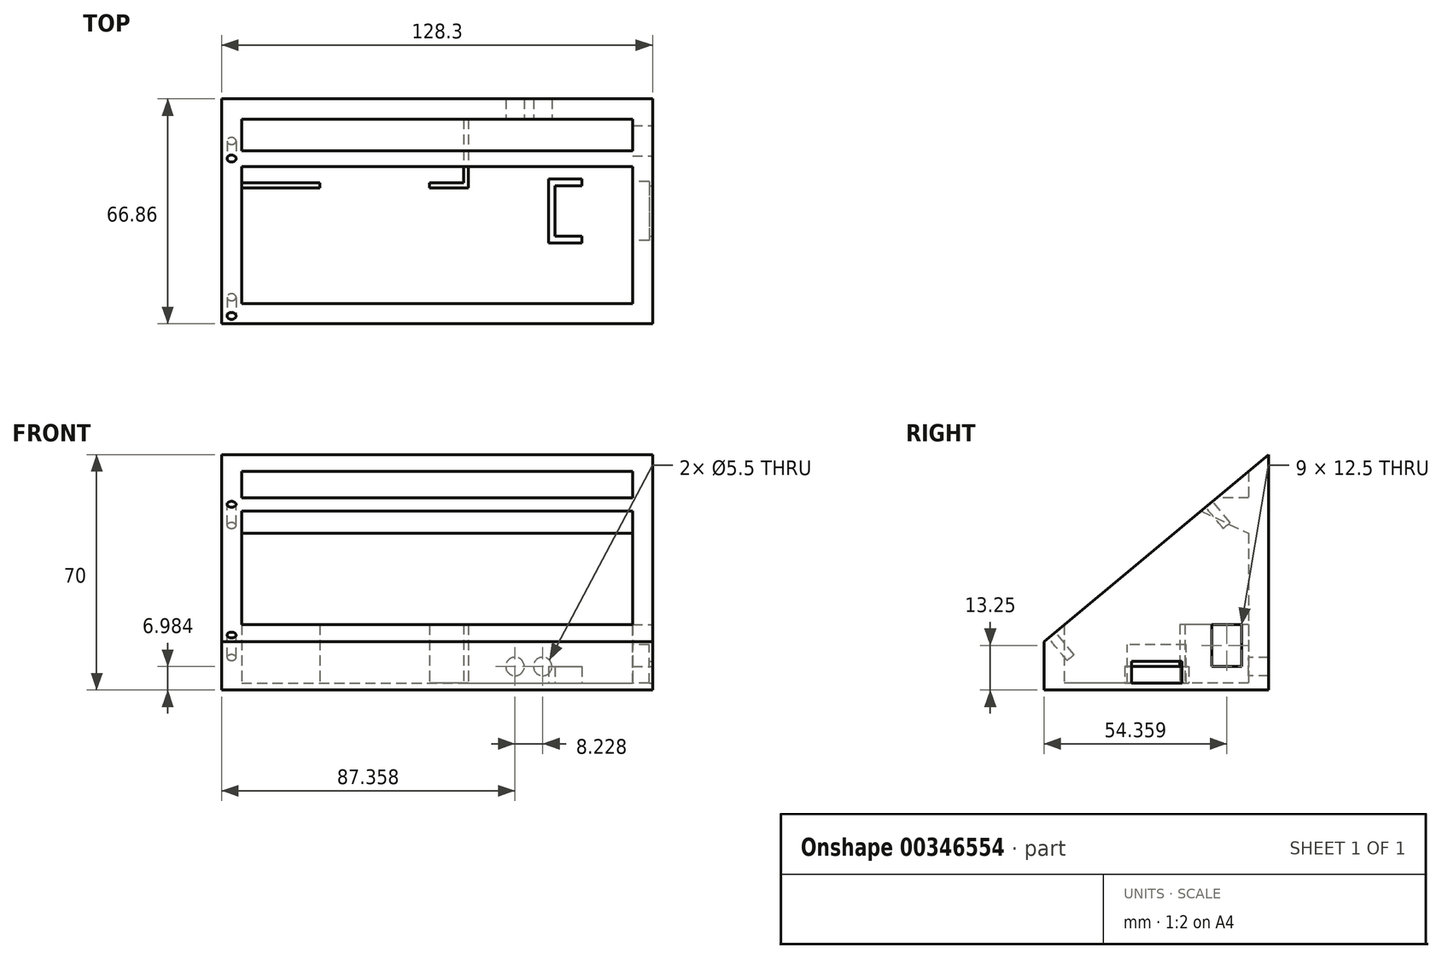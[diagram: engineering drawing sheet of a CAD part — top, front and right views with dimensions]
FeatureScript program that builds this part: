
annotation { "Feature Type Name" : "Feature", "Feature Type Description" : "" }
export const myFeature = defineFeature(function(context is Context, id is Id, definition is map)
    precondition{}
    {
        {
            var Q0;
            Q0=qCreatedBy(makeId("Top.planeOp"),FACE);
            var sketch = newSketch(context, id + "F0", { "sketchPlane" : qUnion([Q0])});
            skLineSegment(sketch, "E0.bottom", {"start": v(-64.15, -33.43) * mm, "end": v(64.15, -33.43) * mm});
            skLineSegment(sketch, "E0.top", {"start": v(-64.15, 33.43) * mm, "end": v(64.15, 33.43) * mm});
            skLineSegment(sketch, "E0.left", {"start": v(-64.15, -33.43) * mm, "end": v(-64.15, 33.43) * mm});
            skLineSegment(sketch, "E0.right", {"start": v(64.15, -33.43) * mm, "end": v(64.15, 33.43) * mm});
            skPoint(sketch, "E0.middle", {"position": v(0, 0) * mm});
            skLineSegment(sketch, "E1.bottom", {"start": v(-58.15, 27.43) * mm, "end": v(58.15, 27.43) * mm});
            skLineSegment(sketch, "E1.top", {"start": v(-58.15, -27.43) * mm, "end": v(58.15, -27.43) * mm});
            skLineSegment(sketch, "E1.left", {"start": v(-58.15, 27.43) * mm, "end": v(-58.15, -27.43) * mm});
            skLineSegment(sketch, "E1.right", {"start": v(58.15, 27.43) * mm, "end": v(58.15, -27.43) * mm});
            skSolve(sketch);
        }
        {
            var Q0;
            Q0=makeQuery(id+"F0.imprint","IMPRINT",FACE,{"disambiguationData":[TD([[makeQuery(id+"F0.imprint","IMPRINT",EDGE,{"derivedFrom":sQuery(id+"F0.wireOp",EDGE,"E0.bottom")}),1.0]])]});
            extrude(context, id + "F1", {"entities" : qUnion([Q0]), "depth" : 70 * mm});
        }
        {
            var Q0;
            Q0=makeQuery(id+"F0.imprint","IMPRINT",FACE,{"disambiguationData":[TD([[makeQuery(id+"F0.imprint","IMPRINT",EDGE,{"derivedFrom":sQuery(id+"F0.wireOp",EDGE,"E1.bottom")}),-1.0]])]});
            extrude(context, id + "F2", {"entities" : qUnion([Q0]), "operationType" : NewBodyOperationType.ADD, "depth" : 2 * mm});
        }
        {
            var Q0;
            Q0=makeQuery(id+"F1.opExtrude","SWEPT_FACE",FACE,{"disambiguationData":[OSD([sQuery(id+"F0.wireOp",EDGE,"E0.right")])]});
            var sketch = newSketch(context, id + "F3", { "sketchPlane" : qUnion([Q0])});
            skLineSegment(sketch, "E2", {"start": v(33.43, 70) * mm, "end": v(-33.43, 14.43) * mm});
            skLineSegment(sketch, "E3", {"start": v(-33.43, 14.43) * mm, "end": v(-33.43, 70) * mm});
            skLineSegment(sketch, "E4", {"start": v(-33.43, 70) * mm, "end": v(33.43, 70) * mm});
            skSolve(sketch);
        }
        {
            var Q0;
            Q0=makeQuery(id+"F3.imprint","IMPRINT",FACE,{"disambiguationData":[TD([[makeQuery(id+"F3.imprint","IMPRINT",EDGE,{"derivedFrom":sQuery(id+"F3.wireOp",EDGE,"E2")}),-1.0]])]});
            extrude(context, id + "F4", {"entities" : qUnion([Q0]), "operationType" : NewBodyOperationType.REMOVE, "oppositeDirection" : true, "depth" : 130 * mm});
        }
        {
            var Q0;
            Q0=makeQuery(id+"F1.opExtrude","SWEPT_FACE",FACE,{"disambiguationData":[OSD([sQuery(id+"F0.wireOp",EDGE,"E0.right")])]});
            var sketch = newSketch(context, id + "F5", { "sketchPlane" : qUnion([Q0])});
            skLineSegment(sketch, "E5.bottom", {"start": v(25.43, 7) * mm, "end": v(16.43, 7) * mm});
            skLineSegment(sketch, "E5.top", {"start": v(25.43, 19.5) * mm, "end": v(16.43, 19.5) * mm});
            skLineSegment(sketch, "E5.left", {"start": v(25.43, 7) * mm, "end": v(25.43, 19.5) * mm});
            skLineSegment(sketch, "E5.right", {"start": v(16.43, 7) * mm, "end": v(16.43, 19.5) * mm});
            skPoint(sketch, "E5.middle", {"position": v(20.93, 13.25) * mm});
            skLineSegment(sketch, "E6.bottom", {"start": v(7.6, 2) * mm, "end": v(-7.4, 2) * mm});
            skLineSegment(sketch, "E6.top", {"start": v(7.6, 8.5) * mm, "end": v(-7.4, 8.5) * mm});
            skLineSegment(sketch, "E6.left", {"start": v(7.6, 2) * mm, "end": v(7.6, 8.5) * mm});
            skLineSegment(sketch, "E6.right", {"start": v(-7.4, 2) * mm, "end": v(-7.4, 8.5) * mm});
            skPoint(sketch, "E6.middle", {"position": v(0.1, 5.25) * mm});
            skSolve(sketch);
        }
        {
            var Q0;
            Q0=makeQuery(id+"F5.imprint","IMPRINT",FACE,{"disambiguationData":[TD([[makeQuery(id+"F5.imprint","IMPRINT",EDGE,{"derivedFrom":sQuery(id+"F5.wireOp",EDGE,"E5.bottom")}),-1.0]])]});
            extrude(context, id + "F6", {"entities" : qUnion([Q0]), "operationType" : NewBodyOperationType.REMOVE, "oppositeDirection" : true, "depth" : 7 * mm});
        }
        {
            var Q0;
            Q0=makeQuery(id+"F5.imprint","IMPRINT",FACE,{"disambiguationData":[TD([[makeQuery(id+"F5.imprint","IMPRINT",EDGE,{"derivedFrom":sQuery(id+"F5.wireOp",EDGE,"E6.bottom")}),-1.0]])]});
            extrude(context, id + "F7", {"entities" : qUnion([Q0]), "operationType" : NewBodyOperationType.REMOVE, "oppositeDirection" : true, "depth" : 7 * mm});
        }
        {
            var Q0;
            Q0=makeQuery(id+"F1.opExtrude","SWEPT_FACE",FACE,{"disambiguationData":[OSD([sQuery(id+"F0.wireOp",EDGE,"E1.right")])]});
            var sketch = newSketch(context, id + "F8", { "sketchPlane" : qUnion([Q0])});
            skLineSegment(sketch, "E7.bottom", {"start": v(-8.84, 2) * mm, "end": v(8.66, 2) * mm});
            skLineSegment(sketch, "E7.top", {"start": v(-8.84, 13.5) * mm, "end": v(8.66, 13.5) * mm});
            skLineSegment(sketch, "E7.left", {"start": v(-8.84, 2) * mm, "end": v(-8.84, 13.5) * mm});
            skLineSegment(sketch, "E7.right", {"start": v(8.66, 2) * mm, "end": v(8.66, 13.5) * mm});
            skSolve(sketch);
        }
        {
            var Q0;
            Q0=makeQuery(id+"F8.imprint","IMPRINT",FACE,{"disambiguationData":[TD([[makeQuery(id+"F8.imprint","IMPRINT",EDGE,{"derivedFrom":sQuery(id+"F8.wireOp",EDGE,"E7.top")}),-1.0]])]});
            extrude(context, id + "F9", {"entities" : qUnion([Q0]), "operationType" : NewBodyOperationType.REMOVE, "oppositeDirection" : true, "depth" : 5 * mm});
        }
        {
            var Q0;
            {var subQ0=sQuery(id+"F8.wireOp",EDGE,"E7.bottom");var subQ1=makeQuery(id+"F7.opExtrude","SWEPT_FACE",FACE,{"disambiguationData":[OSD([sQuery(id+"F5.wireOp",EDGE,"E6.right")])]});var subQ2=sQuery(id+"F0.wireOp",EDGE,"E1.right");var subQ3=makeQuery(id+"F1.opExtrude","SWEPT_FACE",FACE,{"disambiguationData":[OSD([subQ2])]});var subQ4=subQ3;var subQ5=makeQuery(id+"F7.opExtrude","SWEPT_FACE",FACE,{"disambiguationData":[OSD([sQuery(id+"F5.wireOp",EDGE,"E6.bottom")])]});var subQ6=sQuery(id+"F0.wireOp",EDGE,"E1.top");var subQ7=sQuery(id+"F0.wireOp",EDGE,"E1.bottom");var subQ8=makeQuery(id+"F2.opExtrude","CAP_FACE",FACE,{"disambiguationData":[OSD([subQ7,subQ6,sQuery(id+"F0.wireOp",EDGE,"E1.left"),subQ2])],"isStart":false});var subQ10=makeQuery(id+"F7.opExtrude","SWEPT_FACE",FACE,{"disambiguationData":[OSD([sQuery(id+"F5.wireOp",EDGE,"E6.left")])]});Q0=makeQuery(id+"F9.boolean.opBoolean","MERGE",FACE,{"derivedFrom":[makeQuery(id+"F7.boolean.opBoolean","MERGE",FACE,{"derivedFrom":[subQ8,subQ5]}),makeQuery(id+"F9.opExtrude","SWEPT_FACE",FACE,{"disambiguationData":[OSD([subQ0]),TDD([makeQuery(id+"F8.imprint","IMPRINT",EDGE,{"disambiguationData":[TD([[makeQuery(id+"F8.imprint","INTERSECT",VERTEX,{"derivedFrom":[makeQuery(id+"F7.boolean.opBoolean","INTERSECT",EDGE,{"derivedFrom":[subQ4,subQ10]}),subQ0]}),1.0]])],"derivedFrom":subQ0})])]}),makeQuery(id+"F9.opExtrude","SWEPT_FACE",FACE,{"disambiguationData":[OSD([subQ0]),TDD([makeQuery(id+"F8.imprint","IMPRINT",EDGE,{"disambiguationData":[TD([[makeQuery(id+"F8.imprint","INTERSECT",VERTEX,{"derivedFrom":[makeQuery(id+"F7.boolean.opBoolean","INTERSECT",EDGE,{"derivedFrom":[subQ4,subQ1]}),subQ0]}),-1.0]])],"derivedFrom":subQ0})])]})]});}
            var sketch = newSketch(context, id + "F10", { "sketchPlane" : qUnion([Q0])});
            skLineSegment(sketch, "E8.left", {"start": v(33.15, 7.6) * mm, "end": v(33.15, -7.4) * mm});
            skLineSegment(sketch, "E8.right", {"start": v(35.15, 7.6) * mm, "end": v(35.15, -7.4) * mm});
            skLineSegment(sketch, "E9.bottom", {"start": v(35.15, 7.6) * mm, "end": v(43.15, 7.6) * mm});
            skLineSegment(sketch, "E9.top", {"start": v(33.15, 9.6) * mm, "end": v(43.15, 9.6) * mm});
            skLineSegment(sketch, "E9.left", {"start": v(33.15, 7.6) * mm, "end": v(33.15, 9.6) * mm});
            skLineSegment(sketch, "E9.right", {"start": v(43.15, 7.6) * mm, "end": v(43.15, 9.6) * mm});
            skLineSegment(sketch, "E10.bottom", {"start": v(35.15, -7.4) * mm, "end": v(43.15, -7.4) * mm});
            skLineSegment(sketch, "E10.top", {"start": v(33.15, -9.4) * mm, "end": v(43.15, -9.4) * mm});
            skLineSegment(sketch, "E10.left", {"start": v(33.15, -7.4) * mm, "end": v(33.15, -9.4) * mm});
            skLineSegment(sketch, "E10.right", {"start": v(43.15, -7.4) * mm, "end": v(43.15, -9.4) * mm});
            skLineSegment(sketch, "E11", {"start": v(64.15, 7.6) * mm, "end": v(5.36, 7.6) * mm, "construction": true});
            skLineSegment(sketch, "E12", {"start": v(64.15, -7.4) * mm, "end": v(18.59, -7.4) * mm, "construction": true});
            skSolve(sketch);
        }
        {
            var Q0;
            Q0=makeQuery(id+"F10.imprint","IMPRINT",FACE,{"disambiguationData":[TD([[makeQuery(id+"F10.imprint","IMPRINT",EDGE,{"derivedFrom":sQuery(id+"F10.wireOp",EDGE,"E8.left")}),1.0]])]});
            extrude(context, id + "F11", {"entities" : qUnion([Q0]), "operationType" : NewBodyOperationType.ADD, "depth" : 5 * mm});
        }
        {
            var Q0;
            {var subQ0=sQuery(id+"F8.wireOp",EDGE,"E7.bottom");var subQ1=makeQuery(id+"F7.opExtrude","SWEPT_FACE",FACE,{"disambiguationData":[OSD([sQuery(id+"F5.wireOp",EDGE,"E6.right")])]});var subQ2=sQuery(id+"F0.wireOp",EDGE,"E1.right");var subQ3=makeQuery(id+"F1.opExtrude","SWEPT_FACE",FACE,{"disambiguationData":[OSD([subQ2])]});var subQ4=subQ3;var subQ5=makeQuery(id+"F7.opExtrude","SWEPT_FACE",FACE,{"disambiguationData":[OSD([sQuery(id+"F5.wireOp",EDGE,"E6.bottom")])]});var subQ6=sQuery(id+"F0.wireOp",EDGE,"E1.top");var subQ7=sQuery(id+"F0.wireOp",EDGE,"E1.bottom");var subQ8=makeQuery(id+"F2.opExtrude","CAP_FACE",FACE,{"disambiguationData":[OSD([subQ7,subQ6,sQuery(id+"F0.wireOp",EDGE,"E1.left"),subQ2])],"isStart":false});var subQ10=makeQuery(id+"F7.opExtrude","SWEPT_FACE",FACE,{"disambiguationData":[OSD([sQuery(id+"F5.wireOp",EDGE,"E6.left")])]});Q0=makeQuery(id+"F9.boolean.opBoolean","MERGE",FACE,{"derivedFrom":[makeQuery(id+"F7.boolean.opBoolean","MERGE",FACE,{"derivedFrom":[subQ8,subQ5]}),makeQuery(id+"F9.opExtrude","SWEPT_FACE",FACE,{"disambiguationData":[OSD([subQ0]),TDD([makeQuery(id+"F8.imprint","IMPRINT",EDGE,{"disambiguationData":[TD([[makeQuery(id+"F8.imprint","INTERSECT",VERTEX,{"derivedFrom":[makeQuery(id+"F7.boolean.opBoolean","INTERSECT",EDGE,{"derivedFrom":[subQ4,subQ10]}),subQ0]}),1.0]])],"derivedFrom":subQ0})])]}),makeQuery(id+"F9.opExtrude","SWEPT_FACE",FACE,{"disambiguationData":[OSD([subQ0]),TDD([makeQuery(id+"F8.imprint","IMPRINT",EDGE,{"disambiguationData":[TD([[makeQuery(id+"F8.imprint","INTERSECT",VERTEX,{"derivedFrom":[makeQuery(id+"F7.boolean.opBoolean","INTERSECT",EDGE,{"derivedFrom":[subQ4,subQ1]}),subQ0]}),-1.0]])],"derivedFrom":subQ0})])]})]});}
            var sketch = newSketch(context, id + "F12", { "sketchPlane" : qUnion([Q0])});
            skLineSegment(sketch, "E13.bottom", {"start": v(-58.15, 6.93) * mm, "end": v(-34.93, 6.93) * mm});
            skLineSegment(sketch, "E13.top", {"start": v(-58.15, 8.43) * mm, "end": v(-34.93, 8.43) * mm});
            skLineSegment(sketch, "E13.left", {"start": v(-58.15, 8.43) * mm, "end": v(-58.15, 6.93) * mm});
            skLineSegment(sketch, "E13.right", {"start": v(-34.93, 8.43) * mm, "end": v(-34.93, 6.93) * mm});
            skLineSegment(sketch, "E14.bottom", {"start": v(7.85, 27.43) * mm, "end": v(9.35, 27.43) * mm});
            skLineSegment(sketch, "E14.left", {"start": v(7.85, 27.43) * mm, "end": v(7.85, 8.43) * mm});
            skLineSegment(sketch, "E14.right", {"start": v(9.35, 27.43) * mm, "end": v(9.35, 8.43) * mm});
            skLineSegment(sketch, "E15.bottom", {"start": v(7.85, 8.43) * mm, "end": v(-2.25, 8.43) * mm});
            skLineSegment(sketch, "E15.top", {"start": v(9.35, 6.93) * mm, "end": v(-2.25, 6.93) * mm});
            skLineSegment(sketch, "E15.left", {"start": v(9.35, 8.43) * mm, "end": v(9.35, 6.93) * mm});
            skLineSegment(sketch, "E15.right", {"start": v(-2.25, 8.43) * mm, "end": v(-2.25, 6.93) * mm});
            skSolve(sketch);
        }
        {
            var Q0;
            Q0=makeQuery(id+"F12.imprint","IMPRINT",FACE,{"disambiguationData":[TD([[makeQuery(id+"F12.imprint","IMPRINT",EDGE,{"derivedFrom":sQuery(id+"F12.wireOp",EDGE,"E13.bottom")}),1.0]])]});
            var Q1;
            Q1=makeQuery(id+"F12.imprint","IMPRINT",FACE,{"disambiguationData":[TD([[makeQuery(id+"F12.imprint","IMPRINT",EDGE,{"derivedFrom":sQuery(id+"F12.wireOp",EDGE,"E14.bottom")}),-1.0]])]});
            extrude(context, id + "F13", {"entities" : qUnion([Q0, Q1]), "operationType" : NewBodyOperationType.ADD, "depth" : 17.5 * mm});
        }
        {
            var Q0;
            Q0=makeQuery(id+"F4.boolean.opBoolean","COPY",FACE,{"derivedFrom":makeQuery(id+"F4.opExtrude","SWEPT_FACE",FACE,{"disambiguationData":[OSD([sQuery(id+"F3.wireOp",EDGE,"E2")])]})});
            cPlane(context, id + "F14", {"entities" : qUnion([Q0]), "cplaneType" : CPlaneType.OFFSET, "offset" : 0.8 * mm, "width" : 150 * mm, "height" : 150 * mm});
        }
        {
            var Q0;
            Q0=qCreatedBy(id+"F14.planeOp",FACE);
            var sketch = newSketch(context, id + "F15", { "sketchPlane" : qUnion([Q0])});
            skCircle(sketch, "E16", {"center": v(-61.15, 47.37) * mm, "radius": 1.35 * mm});
            skCircle(sketch, "E17", {"center": v(-61.15, -13.48) * mm, "radius": 1.35 * mm});
            skCircle(sketch, "E18.MirrorC", {"center": v(61.15, -13.48) * mm, "radius": 1.35 * mm});
            skCircle(sketch, "E19.MirrorC", {"center": v(61.15, 47.37) * mm, "radius": 1.35 * mm});
            skSolve(sketch);
        }
        {
            var Q0;
            Q0=makeQuery(id+"F15.imprint","IMPRINT",FACE,{"disambiguationData":[TD([[makeQuery(id+"F15.imprint","IMPRINT",EDGE,{"derivedFrom":sQuery(id+"F15.wireOp",EDGE,"E17")}),1.0]])]});
            var Q1;
            Q1=makeQuery(id+"F15.imprint","IMPRINT",FACE,{"disambiguationData":[TD([[makeQuery(id+"F15.imprint","IMPRINT",EDGE,{"derivedFrom":sQuery(id+"F15.wireOp",EDGE,"E18.MirrorC")}),-1.0]])]});
            extrude(context, id + "F16", {"entities" : qUnion([Q0, Q1]), "operationType" : NewBodyOperationType.REMOVE, "oppositeDirection" : true, "depth" : 9.5 * mm});
        }
        {
            var Q0;
            Q0=makeQuery(id+"F1.opExtrude","SWEPT_FACE",FACE,{"disambiguationData":[OSD([sQuery(id+"F0.wireOp",EDGE,"E0.right")])]});
            var sketch = newSketch(context, id + "F17", { "sketchPlane" : qUnion([Q0])});
            skLineSegment(sketch, "E20.bottom", {"start": v(92.05, 115.27) * mm, "end": v(-2.96, 115.27) * mm});
            skLineSegment(sketch, "E20.top", {"start": v(92.05, 57.17) * mm, "end": v(-2.96, 57.17) * mm});
            skLineSegment(sketch, "E20.left", {"start": v(92.05, 115.27) * mm, "end": v(92.05, 57.17) * mm});
            skLineSegment(sketch, "E20.right", {"start": v(-2.96, 115.27) * mm, "end": v(-2.96, 57.17) * mm});
            skPoint(sketch, "E21", {"position": v(17.99, 57.17) * mm});
            skSolve(sketch);
        }
        {
            var Q0;
            Q0=makeQuery(id+"F17.imprint","IMPRINT",FACE,{"disambiguationData":[TD([[makeQuery(id+"F17.imprint","IMPRINT",EDGE,{"derivedFrom":sQuery(id+"F17.wireOp",EDGE,"E20.bottom")}),1.0]])]});
            extrude(context, id + "F18", {"entities" : qUnion([Q0]), "operationType" : NewBodyOperationType.REMOVE, "oppositeDirection" : true, "depth" : 141.4 * mm});
        }
        {
            var Q0;
            {var subQ0=sQuery(id+"F17.wireOp",EDGE,"E20.top");var subQ3=makeQuery(id+"F4.boolean.opBoolean","COPY",EDGE,{"derivedFrom":makeQuery(id+"F4.opExtrude","CAP_EDGE",EDGE,{"disambiguationData":[OSD([sQuery(id+"F3.wireOp",EDGE,"E2")])],"isStart":true})});var subQ4=makeQuery(id+"F17.imprint","INTERSECT",VERTEX,{"derivedFrom":[subQ3,subQ0]});Q0=makeQuery(id+"F17.imprint","IMPRINT",FACE,{"disambiguationData":[TD([[makeQuery(id+"F17.imprint","IMPRINT",EDGE,{"disambiguationData":[TD([[subQ4,1.0]])],"derivedFrom":subQ0}),-1.0]])]});}
            extrude(context, id + "F19", {"entities" : qUnion([Q0]), "operationType" : NewBodyOperationType.REMOVE, "oppositeDirection" : true, "depth" : 133.9 * mm});
        }
        {
            var Q0;
            Q0=makeQuery(id+"F1.opExtrude","SWEPT_FACE",FACE,{"disambiguationData":[OSD([sQuery(id+"F0.wireOp",EDGE,"E0.right")])]});
            var sketch = newSketch(context, id + "F20", { "sketchPlane" : qUnion([Q0])});
            skLineSegment(sketch, "E22", {"start": v(13.28, 53.25) * mm, "end": v(33.43, 43.78) * mm});
            skLineSegment(sketch, "E23", {"start": v(33.43, 43.78) * mm, "end": v(33.43, 57.17) * mm});
            skLineSegment(sketch, "E24", {"start": v(33.43, 57.17) * mm, "end": v(17.99, 57.17) * mm});
            skLineSegment(sketch, "E25", {"start": v(17.99, 57.17) * mm, "end": v(13.28, 53.25) * mm});
            skSolve(sketch);
        }
        {
            var Q0;
            Q0=makeQuery(id+"F20.imprint","IMPRINT",FACE,{"disambiguationData":[TD([[makeQuery(id+"F20.imprint","IMPRINT",EDGE,{"derivedFrom":sQuery(id+"F20.wireOp",EDGE,"E22")}),1.0]])]});
            extrude(context, id + "F21", {"entities" : qUnion([Q0]), "operationType" : NewBodyOperationType.ADD, "oppositeDirection" : true, "depth" : 128.26 * mm});
        }
        {
            var Q0;
            Q0=makeQuery(id+"F15.imprint","IMPRINT",FACE,{"disambiguationData":[TD([[makeQuery(id+"F15.imprint","IMPRINT",EDGE,{"derivedFrom":sQuery(id+"F15.wireOp",EDGE,"E19.MirrorC")}),-1.0]])]});
            var Q1;
            Q1=makeQuery(id+"F15.imprint","IMPRINT",FACE,{"disambiguationData":[TD([[makeQuery(id+"F15.imprint","IMPRINT",EDGE,{"derivedFrom":sQuery(id+"F15.wireOp",EDGE,"E16")}),1.0]])]});
            extrude(context, id + "F22", {"entities" : qUnion([Q0, Q1]), "operationType" : NewBodyOperationType.REMOVE, "oppositeDirection" : true, "depth" : 9 * mm});
        }
        {
            var Q0;
            Q0=makeQuery(id+"F1.opExtrude","SWEPT_FACE",FACE,{"disambiguationData":[OSD([sQuery(id+"F0.wireOp",EDGE,"E1.bottom")])]});
            var sketch = newSketch(context, id + "F23", { "sketchPlane" : qUnion([Q0])});
            skCircle(sketch, "E26", {"center": v(23.2, 6.98) * mm, "radius": 2.75 * mm});
            skCircle(sketch, "E27", {"center": v(31.44, 6.98) * mm, "radius": 2.75 * mm});
            skLineSegment(sketch, "E28", {"start": v(23.2, 6.98) * mm, "end": v(31.44, 6.98) * mm, "construction": true});
            skSolve(sketch);
        }
        {
            var Q0;
            Q0=makeQuery(id+"F23.imprint","IMPRINT",FACE,{"disambiguationData":[TD([[makeQuery(id+"F23.imprint","IMPRINT",EDGE,{"derivedFrom":sQuery(id+"F23.wireOp",EDGE,"E26")}),1.0]])]});
            var Q1;
            Q1=makeQuery(id+"F23.imprint","IMPRINT",FACE,{"disambiguationData":[TD([[makeQuery(id+"F23.imprint","IMPRINT",EDGE,{"derivedFrom":sQuery(id+"F23.wireOp",EDGE,"E27")}),1.0]])]});
            extrude(context, id + "F24", {"entities" : qUnion([Q0, Q1]), "operationType" : NewBodyOperationType.REMOVE, "oppositeDirection" : true, "depth" : 25 * mm});
        }
    });
